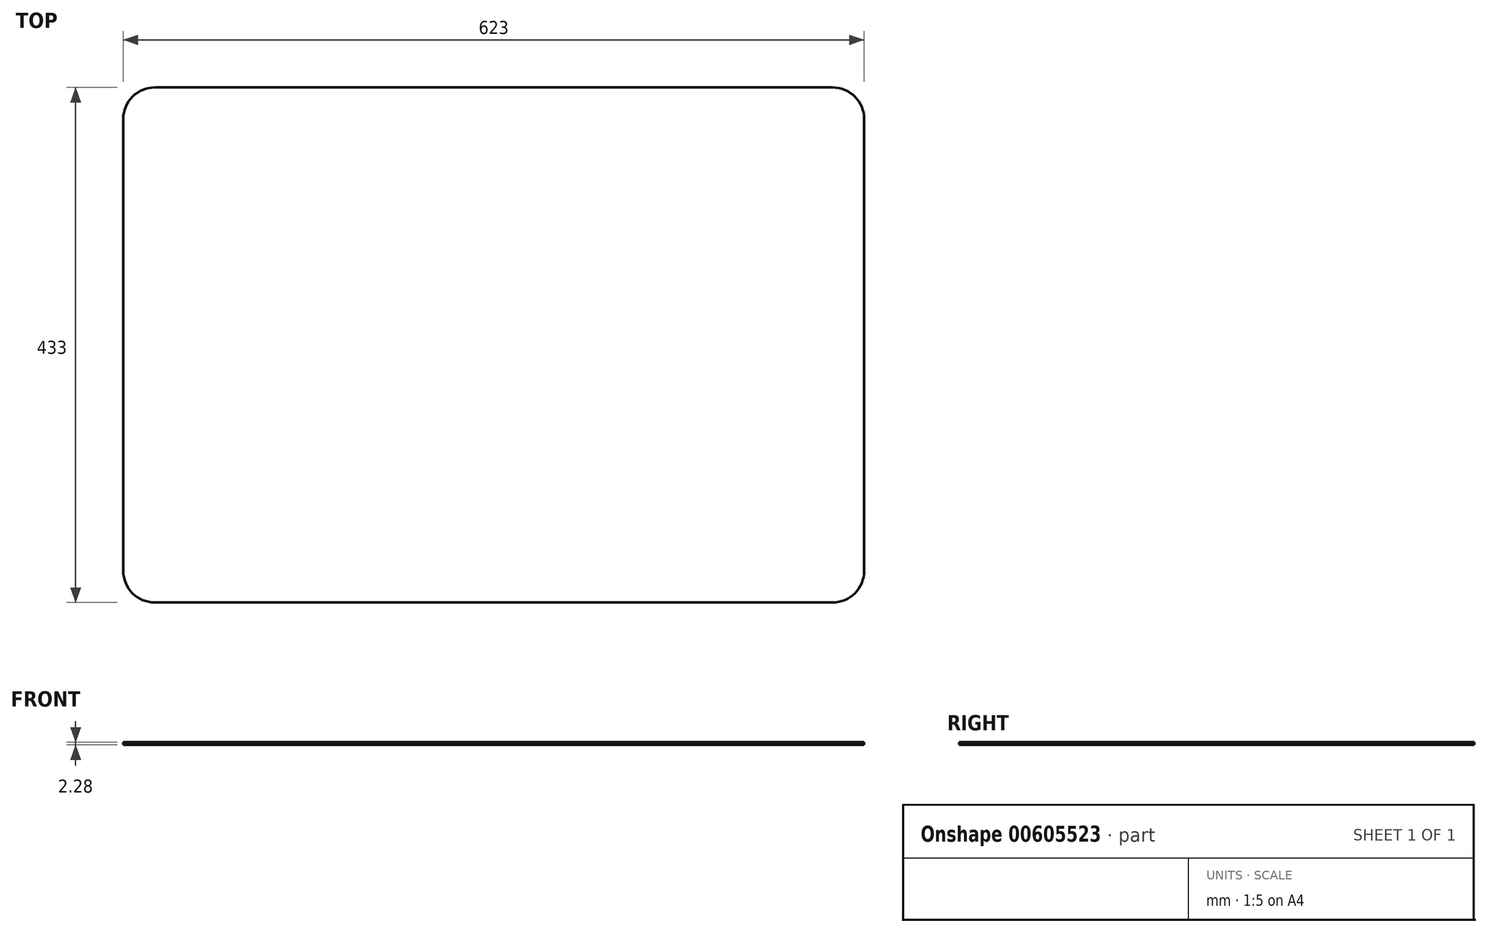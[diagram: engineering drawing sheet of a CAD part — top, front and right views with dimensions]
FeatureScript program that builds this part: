
annotation { "Feature Type Name" : "Feature", "Feature Type Description" : "" }
export const myFeature = defineFeature(function(context is Context, id is Id, definition is map)
    precondition{}
    {
        {
            var Q0;
            Q0=qCreatedBy(makeId("Top.planeOp"),FACE);
            var sketch = newSketch(context, id + "F0", { "sketchPlane" : qUnion([Q0])});
            skLineSegment(sketch, "E0.bottom", {"start": v(-285, -216.5) * mm, "end": v(285, -216.5) * mm});
            skLineSegment(sketch, "E0.top", {"start": v(-285, 216.5) * mm, "end": v(285, 216.5) * mm});
            skLineSegment(sketch, "E0.left", {"start": v(-311.5, -190) * mm, "end": v(-311.5, 190) * mm});
            skLineSegment(sketch, "E0.right", {"start": v(311.5, -190) * mm, "end": v(311.5, 190) * mm});
            skPoint(sketch, "E0.middle", {"position": v(0, 0) * mm});
            skPoint(sketch, "E1.visualSharp", {"position": v(-311.5, 216.5) * mm});
            skArc(sketch, "E1.filletArc", {"start": v(-285, 216.5) * mm, "mid": v(-303.74, 208.74) * mm, "end": v(-311.5, 190) * mm});
            skPoint(sketch, "E2.visualSharp", {"position": v(-311.5, -216.5) * mm});
            skArc(sketch, "E2.filletArc", {"start": v(-311.5, -190) * mm, "mid": v(-303.74, -208.74) * mm, "end": v(-285, -216.5) * mm});
            skPoint(sketch, "E3.visualSharp", {"position": v(311.5, -216.5) * mm});
            skArc(sketch, "E3.filletArc", {"start": v(285, -216.5) * mm, "mid": v(303.74, -208.74) * mm, "end": v(311.5, -190) * mm});
            skPoint(sketch, "E4.visualSharp", {"position": v(311.5, 216.5) * mm});
            skArc(sketch, "E4.filletArc", {"start": v(311.5, 190) * mm, "mid": v(303.74, 208.74) * mm, "end": v(285, 216.5) * mm});
            skSolve(sketch);
        }
        {
            var Q0;
            Q0=makeQuery(id+"F0.imprint","IMPRINT",FACE,{"disambiguationData":[TD([[makeQuery(id+"F0.imprint","IMPRINT",EDGE,{"derivedFrom":sQuery(id+"F0.wireOp",EDGE,"E0.bottom")}),1.0]])]});
            extrude(context, id + "F1", {"entities" : qUnion([Q0]), "depth" : 2.28 * mm, "offsetDistance" : 25 * mm});
        }
    });
